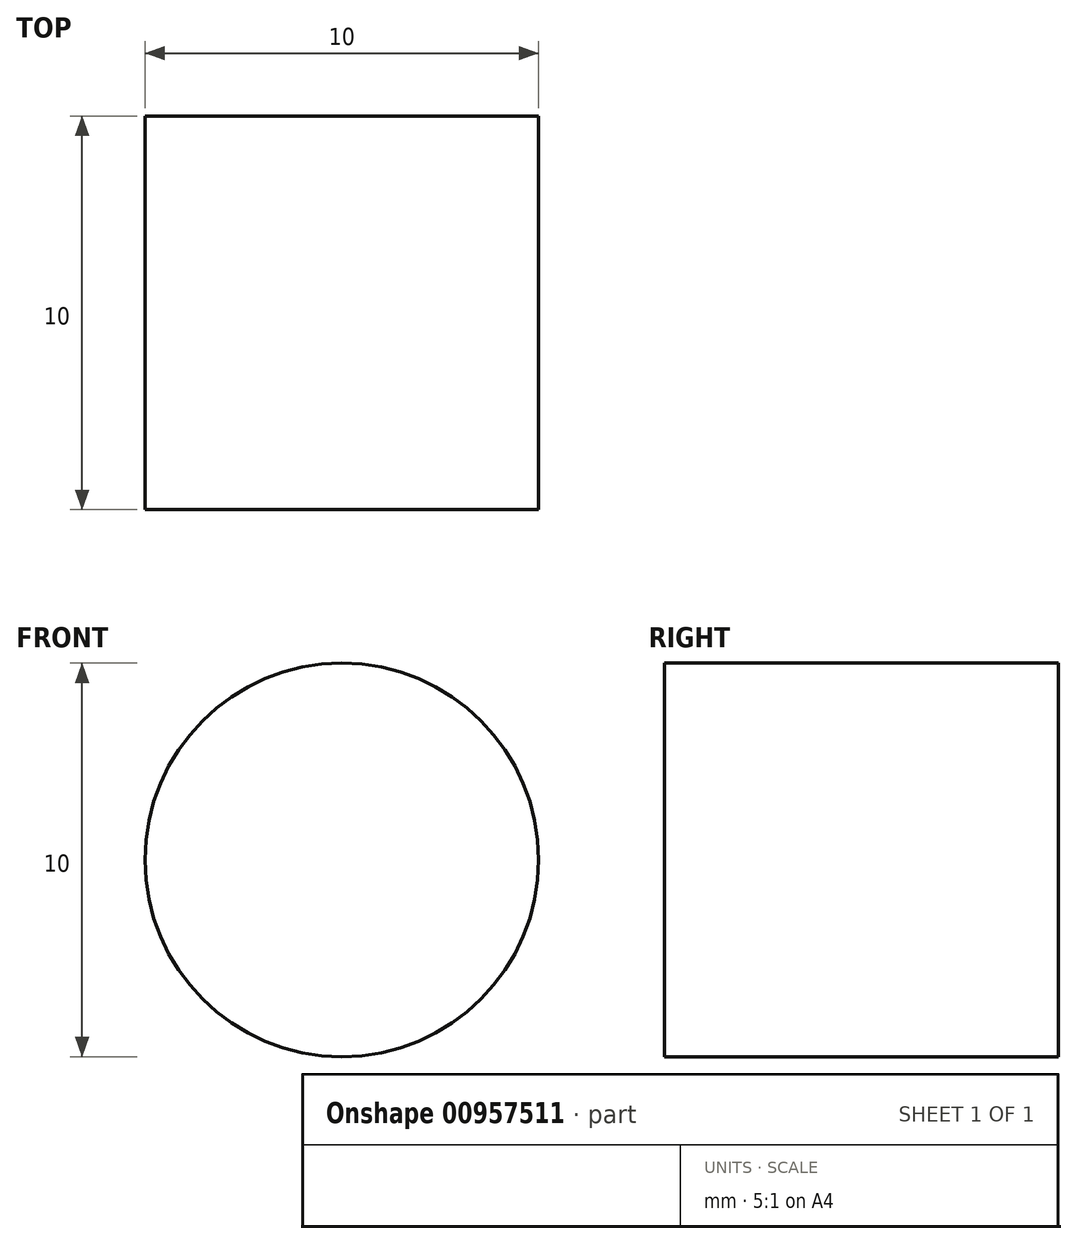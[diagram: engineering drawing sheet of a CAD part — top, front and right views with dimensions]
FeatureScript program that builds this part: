
annotation { "Feature Type Name" : "Feature", "Feature Type Description" : "" }
export const myFeature = defineFeature(function(context is Context, id is Id, definition is map)
    precondition{}
    {
        {
            var Q0;
            Q0=qCreatedBy(makeId("Front.planeOp"),FACE);
            var sketch = newSketch(context, id + "F0", { "sketchPlane" : qUnion([Q0])});
            skCircle(sketch, "E0", {"center": v(-44.47, 25.82) * mm, "radius": 5 * mm});
            skSolve(sketch);
        }
        {
            var Q0;
            Q0=makeQuery(id+"F0.imprint","IMPRINT",FACE,{"disambiguationData":[TD([[makeQuery(id+"F0.imprint","IMPRINT",EDGE,{"derivedFrom":sQuery(id+"F0.wireOp",EDGE,"E0")}),1.0]])]});
            extrude(context, id + "F1", {"entities" : qUnion([Q0]), "depth" : 10 * mm, "offsetDistance" : 25 * mm});
        }
    });
